annotation { "Feature Type Name" : "Feature", "Feature Type Description" : "" }
export const myFeature = defineFeature(function(context is Context, id is Id, definition is map)
    precondition{}
    {
        {
            var Q0;
            Q0=qCreatedBy(makeId("Front.planeOp"),FACE);
            var sketch = newSketch(context, id + "F0", { "sketchPlane" : qUnion([Q0])});
            skCircle(sketch, "E0", {"center": v(-37.42, 25.8) * mm, "radius": 6.35 * mm});
            skCircle(sketch, "E1", {"center": v(-37.42, 25.8) * mm, "radius": 38.1 * mm});
            skLineSegment(sketch, "E2", {"start": v(26.6, 49.53) * mm, "end": v(19.58, 33.3) * mm});
            skLineSegment(sketch, "E3", {"start": v(19.58, 33.3) * mm, "end": v(45.01, 33.3) * mm});
            skLineSegment(sketch, "E4", {"start": v(45.01, 33.3) * mm, "end": v(39.31, 49.97) * mm});
            skLineSegment(sketch, "E5", {"start": v(39.31, 49.97) * mm, "end": v(26.6, 49.53) * mm});
            skLineSegment(sketch, "E6", {"start": v(39.31, 49.97) * mm, "end": v(45.01, 33.3) * mm});
            skCircle(sketch, "E7", {"center": v(21.56, -1.95) * mm, "radius": 7.62 * mm});
            skSolve(sketch);
        }
        {
            var Q0;
            Q0 = qSketchRegion(id + "F0", true);
            extrude(context, id + "F1", {"entities" : qUnion([Q0]), "depth" : 12.7 * mm});
        }
        {
            var Q0;
            Q0=makeQuery(id+"F0.imprint","IMPRINT",FACE,{"disambiguationData":[TD([[makeQuery(id+"F0.imprint","IMPRINT",EDGE,{"derivedFrom":sQuery(id+"F0.wireOp",EDGE,"E2")}),1.0]])]});
            extrude(context, id + "F2", {"entities" : qUnion([Q0]), "operationType" : NewBodyOperationType.ADD, "depth" : 2.54 * mm});
        }
        {
            var Q0;
            Q0 = qSketchRegion(id + "F0", true);
            extrude(context, id + "F3", {"entities" : qUnion([Q0]), "depth" : 457200 * mm});
        }
    });